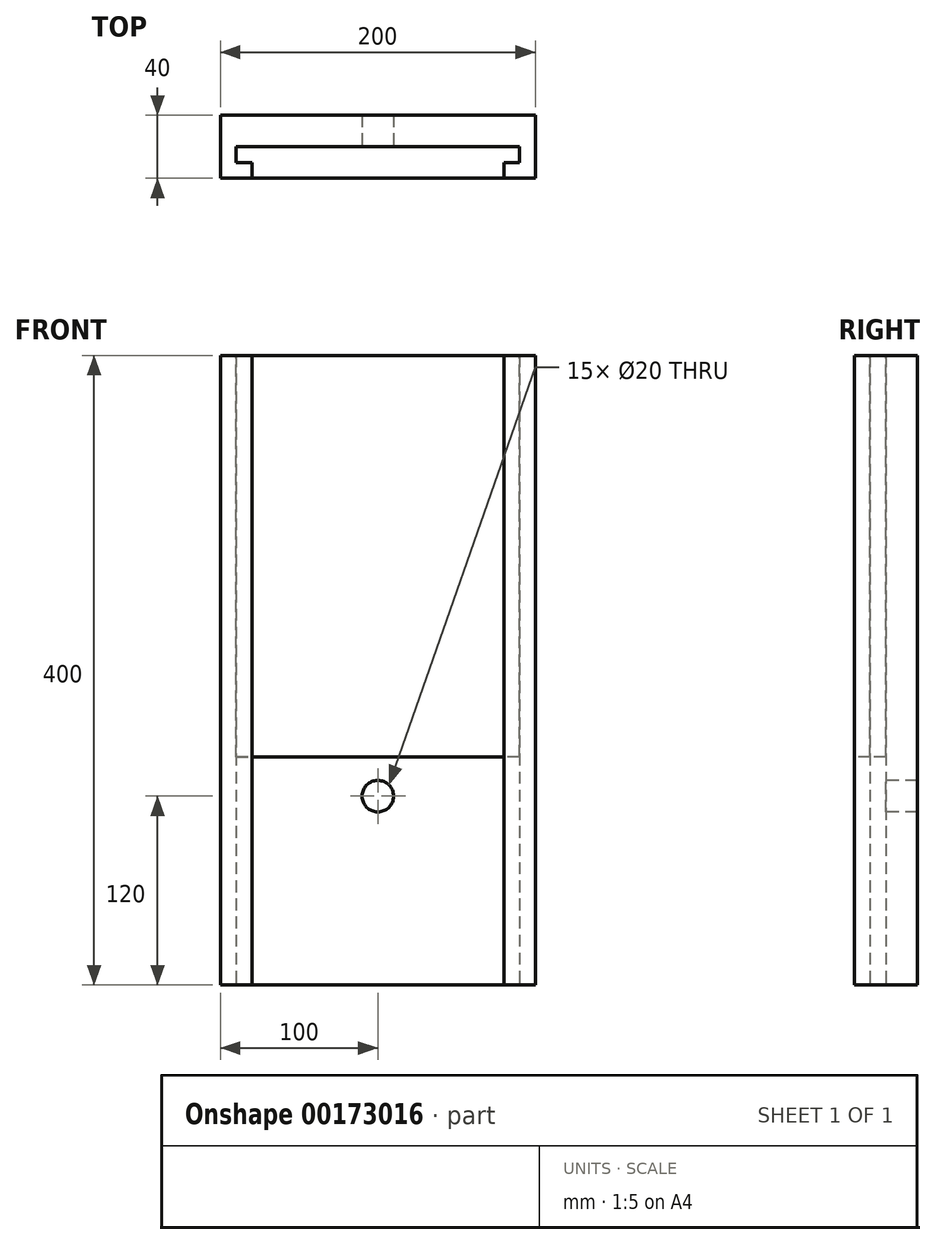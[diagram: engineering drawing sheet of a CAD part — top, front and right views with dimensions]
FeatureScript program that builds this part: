
annotation { "Feature Type Name" : "Feature", "Feature Type Description" : "" }
export const myFeature = defineFeature(function(context is Context, id is Id, definition is map)
    precondition{}
    {
        {
            var Q0;
            Q0=qCreatedBy(makeId("Top.planeOp"),FACE);
            var sketch = newSketch(context, id + "F0", { "sketchPlane" : qUnion([Q0])});
            skLineSegment(sketch, "E0", {"start": v(0, 20) * mm, "end": v(90, 20) * mm});
            skLineSegment(sketch, "E1", {"start": v(90, 20) * mm, "end": v(90, 10) * mm});
            skLineSegment(sketch, "E2", {"start": v(90, 10) * mm, "end": v(80, 10) * mm});
            skLineSegment(sketch, "E3", {"start": v(80, 10) * mm, "end": v(80, 0) * mm});
            skLineSegment(sketch, "E4", {"start": v(80, 0) * mm, "end": v(100, 0) * mm});
            skLineSegment(sketch, "E5", {"start": v(100, 0) * mm, "end": v(100, 40) * mm});
            skLineSegment(sketch, "E6", {"start": v(100, 40) * mm, "end": v(0, 40) * mm});
            skLineSegment(sketch, "E7", {"start": v(0, 40) * mm, "end": v(0, 0) * mm, "construction": true});
            skLineSegment(sketch, "E8.MirrorCS", {"start": v(0, 20) * mm, "end": v(-90, 20) * mm});
            skLineSegment(sketch, "E9.MirrorCS", {"start": v(-90, 20) * mm, "end": v(-90, 10) * mm});
            skLineSegment(sketch, "E10.MirrorCS", {"start": v(-90, 10) * mm, "end": v(-80, 10) * mm});
            skLineSegment(sketch, "E11.MirrorCS", {"start": v(-80, 10) * mm, "end": v(-80, 0) * mm});
            skLineSegment(sketch, "E12.MirrorCS", {"start": v(-80, 0) * mm, "end": v(-100, 0) * mm});
            skLineSegment(sketch, "E13.MirrorCS", {"start": v(-100, 0) * mm, "end": v(-100, 40) * mm});
            skLineSegment(sketch, "E14.MirrorCS", {"start": v(-100, 40) * mm, "end": v(0, 40) * mm});
            skSolve(sketch);
        }
        {
            var Q0;
            Q0=makeQuery(id+"F0.imprint","IMPRINT",FACE,{"disambiguationData":[TD([[makeQuery(id+"F0.imprint","IMPRINT",EDGE,{"derivedFrom":sQuery(id+"F0.wireOp",EDGE,"E0")}),1.0]])]});
            extrude(context, id + "F1", {"entities" : qUnion([Q0]), "depth" : 280 * mm, "hasSecondDirection" : true, "secondDirectionOppositeDirection" : true, "secondDirectionDepth" : 120 * mm});
        }
        {
            var Q0;
            Q0=makeQuery(id+"F1.opExtrude","SWEPT_FACE",FACE,{"disambiguationData":[OSD([sQuery(id+"F0.wireOp",EDGE,"E0"),sQuery(id+"F0.wireOp",EDGE,"E8.MirrorCS")])]});
            var sketch = newSketch(context, id + "F2", { "sketchPlane" : qUnion([Q0])});
            skCircle(sketch, "E15", {"center": v(0, 0) * mm, "radius": 10 * mm});
            skSolve(sketch);
        }
        {
            var Q0;
            Q0=qSketchRegion(id+"F2",true);
            extrude(context, id + "F3", {"entities" : qUnion([Q0]), "operationType" : NewBodyOperationType.REMOVE, "oppositeDirection" : true, "depth" : 20 * mm});
        }
        {
            var Q0;
            Q0=makeQuery(id+"F1.opExtrude","CAP_FACE",FACE,{"disambiguationData":[OSD([sQuery(id+"F0.wireOp",EDGE,"E0"),sQuery(id+"F0.wireOp",EDGE,"E1"),sQuery(id+"F0.wireOp",EDGE,"E2"),sQuery(id+"F0.wireOp",EDGE,"E3"),sQuery(id+"F0.wireOp",EDGE,"E4"),sQuery(id+"F0.wireOp",EDGE,"E5"),sQuery(id+"F0.wireOp",EDGE,"E6"),sQuery(id+"F0.wireOp",EDGE,"E8.MirrorCS"),sQuery(id+"F0.wireOp",EDGE,"E9.MirrorCS"),sQuery(id+"F0.wireOp",EDGE,"E10.MirrorCS"),sQuery(id+"F0.wireOp",EDGE,"E11.MirrorCS"),sQuery(id+"F0.wireOp",EDGE,"E12.MirrorCS"),sQuery(id+"F0.wireOp",EDGE,"E13.MirrorCS"),sQuery(id+"F0.wireOp",EDGE,"E14.MirrorCS")])],"isStart":false});
            var sketch = newSketch(context, id + "F4", { "sketchPlane" : qUnion([Q0])});
            skLineSegment(sketch, "E16", {"start": v(-80, 0) * mm, "end": v(-80, 10) * mm});
            skLineSegment(sketch, "E17", {"start": v(-80, 10) * mm, "end": v(-90, 10) * mm});
            skLineSegment(sketch, "E18", {"start": v(-90, 10) * mm, "end": v(-90, 20) * mm});
            skLineSegment(sketch, "E19", {"start": v(-90, 20) * mm, "end": v(90, 20) * mm});
            skLineSegment(sketch, "E20", {"start": v(90, 20) * mm, "end": v(90, 10) * mm});
            skLineSegment(sketch, "E21", {"start": v(90, 10) * mm, "end": v(80, 10) * mm});
            skLineSegment(sketch, "E22", {"start": v(80, 10) * mm, "end": v(80, 0) * mm});
            skLineSegment(sketch, "E23", {"start": v(80, 0) * mm, "end": v(-80, 0) * mm});
            skSolve(sketch);
        }
        {
            var Q0;
            Q0=makeQuery(id+"F4.imprint","IMPRINT",FACE,{"disambiguationData":[TD([[makeQuery(id+"F4.imprint","IMPRINT",EDGE,{"derivedFrom":sQuery(id+"F4.wireOp",EDGE,"E16")}),1.0]])]});
            extrude(context, id + "F5", {"entities" : qUnion([Q0]), "oppositeDirection" : true, "depth" : 255 * mm});
        }
    });
